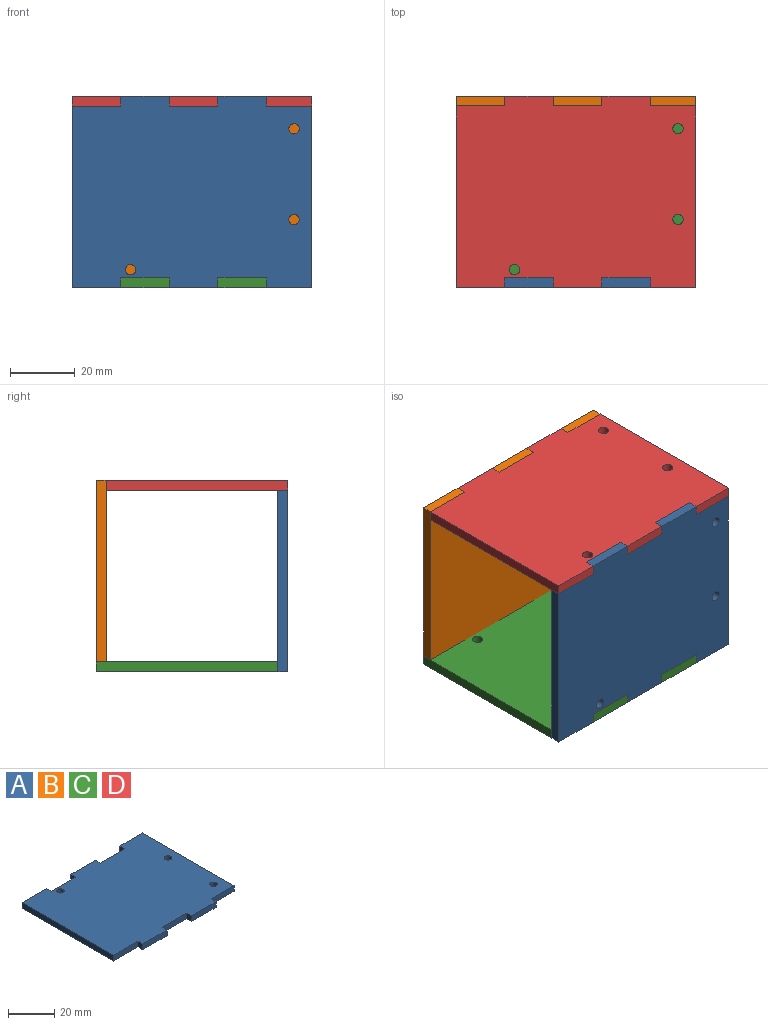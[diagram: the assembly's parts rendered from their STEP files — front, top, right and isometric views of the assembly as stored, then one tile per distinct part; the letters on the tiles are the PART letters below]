
ASSEMBLY  parts=4 mates=3
PART A: 25 faces, bbox 74x59x3 mm
  f0: plane 56x3mm, normal (-1,0,0), area 168mm2, adj f1,f22,f23,f24
  f1: plane 15x3mm, normal (0,-1,0), area 45mm2, adj f0,f2,f23,f24
  f2: plane 3x3mm, normal (-1,0,0), area 9mm2, adj f1,f3,f23,f24
  f3: plane 15x3mm, normal (0,-1,0), area 45mm2, adj f2,f4,f23,f24
  f4: plane 3x3mm, normal (1,0,0), area 9mm2, adj f3,f5,f23,f24
  f5: plane 15x3mm, normal (0,-1,0), area 45mm2, adj f4,f6,f23,f24
  f6: plane 3x3mm, normal (-1,0,0), area 9mm2, adj f5,f7,f23,f24
  f7: plane 15x3mm, normal (0,-1,0), area 45mm2, adj f6,f8,f23,f24
  f8: plane 3x3mm, normal (1,0,0), area 9mm2, adj f7,f9,f23,f24
  f9: plane 14x3mm, normal (0,-1,0), area 42mm2, adj f8,f10,f23,f24
  f10: plane 56x3mm, normal (1,0,0), area 168mm2, adj f9,f11,f23,f24
  f11: plane 14x3mm, normal (0,1,0), area 42mm2, adj f10,f12,f23,f24
  f12: plane 3x3mm, normal (-1,0,0), area 9mm2, adj f11,f13,f23,f24
  f13: plane 15x3mm, normal (0,1,0), area 45mm2, adj f12,f14,f23,f24
  f14: plane 3x3mm, normal (1,0,0), area 9mm2, adj f13,f15,f23,f24
  f15: plane 15x3mm, normal (0,1,0), area 45mm2, adj f14,f16,f23,f24
  f16: plane 3x3mm, normal (-1,0,0), area 9mm2, adj f15,f17,f23,f24
  f17: plane 15x3mm, normal (0,1,0), area 45mm2, adj f16,f18,f23,f24
  f18: plane 3x3mm, normal (1,0,0), area 9mm2, adj f17,f22,f23,f24
  f19: cylinder r=1.6mm len=3.2mm, axis (0,0,-1), area 30.2mm2, adj f23,f24
  f20: cylinder r=1.6mm len=3.2mm, axis (0,0,-1), area 30.2mm2, adj f23,f24
  f21: cylinder r=1.6mm len=3.2mm, axis (0,0,-1), area 30.2mm2, adj f23,f24
  f22: plane 15x3mm, normal (0,1,0), area 45mm2, adj f0,f18,f23,f24
  f23: plane 74x59mm, normal (0,0,1), area 4119.9mm2, adj f0,f1,f2,f3,f4,f5,f6,f7
  f24: plane 74x59mm, normal (0,0,-1), area 4119.9mm2, adj f0,f1,f2,f3,f4,f5,f6,f7
PART B: same geometry as A
PART C: same geometry as A
PART D: same geometry as A
PLACE A rot(axis=(-1,0,0),90deg) t=(-3.26,-61.38,38.62)mm
PLACE B rot(axis=(1,0,0),90deg) t=(-3.26,-2.38,38.62)mm
PLACE C t=(-3.26,-31.88,9.12)mm
PLACE D rot(axis=(-1,0,0),180deg) t=(-3.26,-31.88,68.12)mm
MATE fastened D.f2 <-> B.f18  axis (-1,0,0) through (-25.26,-3.88,66.62)mm
MATE fastened B.f2 <-> C.f18  axis (-1,0,0) through (-25.26,-3.88,10.62)mm
MATE fastened D.f18 <-> A.f2  axis (1,0,0) through (-25.26,-59.88,66.62)mm
